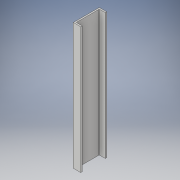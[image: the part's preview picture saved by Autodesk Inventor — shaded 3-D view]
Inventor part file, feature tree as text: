
AUTODESK INVENTOR PART (.ipt)
format: ipt  version: 2019 (Build 230136000, 136)  size: 113,664 bytes
history: native  units: mm
features: extrude x2, sketch x2, fillet x1
ambient origin geometry x8: Origin, YZ Plane, XZ Plane, XY Plane, X Axis, Y Axis, Z Axis, Center Point
bodies: Solid1 (feature_tree)
feature tree (5):
  extrude  "Extrusion1"  Depth=175.0mm
  extrude  "Extrusion2"  Depth=155.0mm
  fillet  "Fillet1"  Radius=40.0mm
  sketch  "Sketch1"  dims[d0=850.0mm d1=175.0mm]
  sketch  "Sketch2"  dims[d2=50.0mm d3=0.0mm d4=155.0mm d5=40.0mm d6=0.0mm d7=4.0mm]
